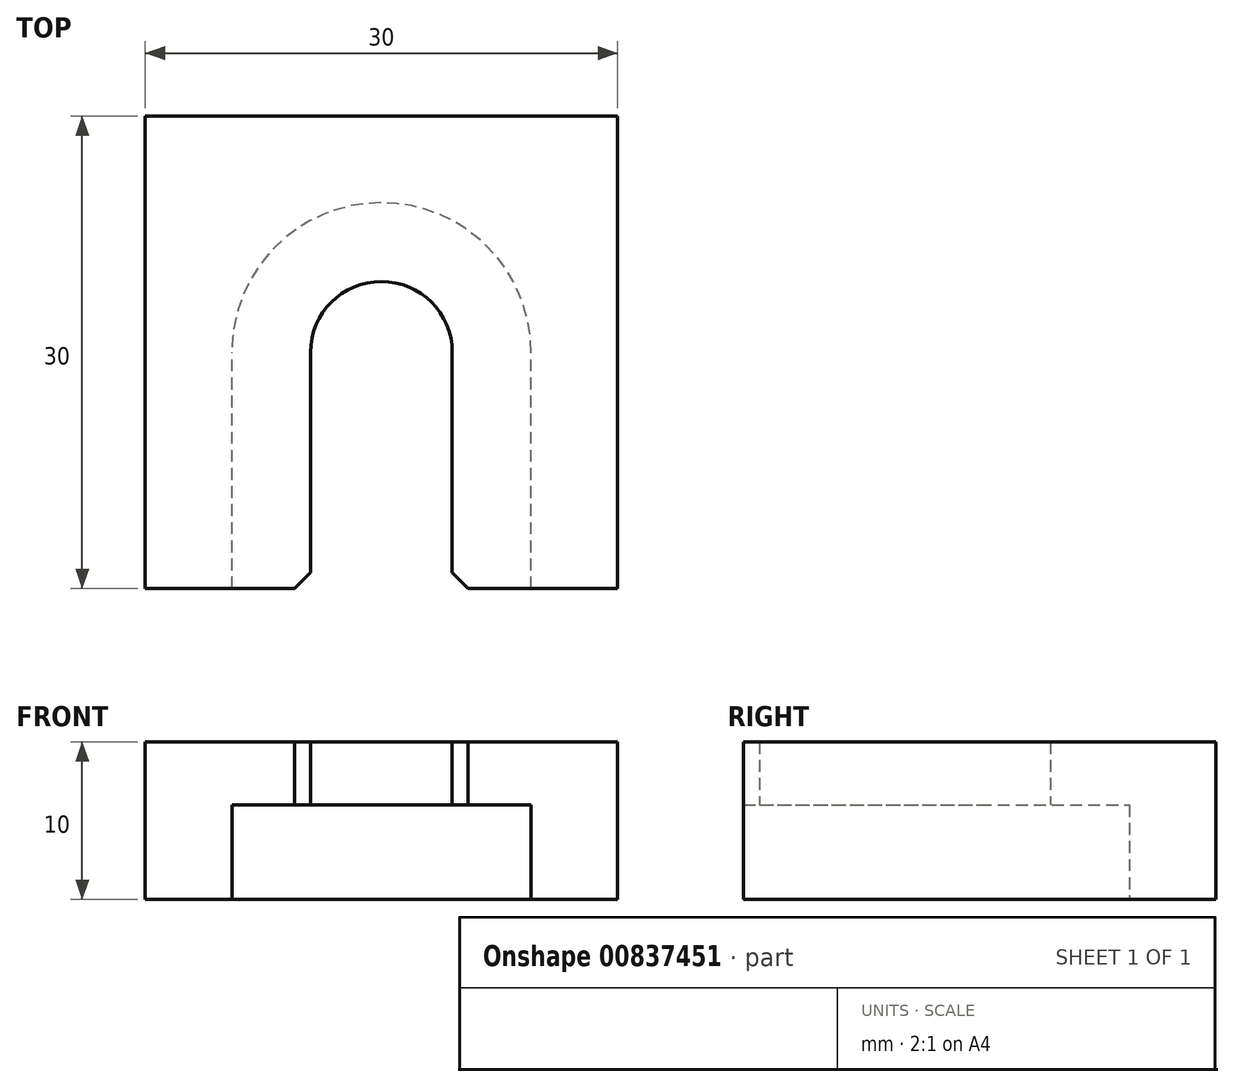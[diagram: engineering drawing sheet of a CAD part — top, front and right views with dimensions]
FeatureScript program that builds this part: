
annotation { "Feature Type Name" : "Feature", "Feature Type Description" : "" }
export const myFeature = defineFeature(function(context is Context, id is Id, definition is map)
    precondition{}
    {
        {
            var Q0;
            Q0=qCreatedBy(makeId("Top.planeOp"),FACE);
            var sketch = newSketch(context, id + "F0", { "sketchPlane" : qUnion([Q0])});
            skLineSegment(sketch, "E0.bottom", {"start": v(-15, 0) * mm, "end": v(-4.5, 0) * mm});
            skLineSegment(sketch, "E0.top", {"start": v(-15, 30) * mm, "end": v(15, 30) * mm});
            skLineSegment(sketch, "E0.left", {"start": v(-15, 0) * mm, "end": v(-15, 30) * mm});
            skLineSegment(sketch, "E0.right", {"start": v(15, 0) * mm, "end": v(15, 30) * mm});
            skLineSegment(sketch, "E1", {"start": v(-4.5, 0) * mm, "end": v(-4.5, 15) * mm});
            skLineSegment(sketch, "E2", {"start": v(4.5, 0) * mm, "end": v(4.5, 15) * mm});
            skArc(sketch, "E3", {"start": v(4.5, 15) * mm, "mid": v(0, 19.5) * mm, "end": v(-4.5, 15) * mm});
            skLineSegment(sketch, "E4.trimOffspring", {"start": v(4.5, 0) * mm, "end": v(15, 0) * mm});
            skSolve(sketch);
        }
        {
            var Q0;
            Q0=makeQuery(id+"F0.imprint","IMPRINT",FACE,{"disambiguationData":[TD([[makeQuery(id+"F0.imprint","IMPRINT",EDGE,{"derivedFrom":sQuery(id+"F0.wireOp",EDGE,"E0.bottom")}),1.0]])]});
            extrude(context, id + "F1", {"entities" : qUnion([Q0]), "depth" : 10 * mm, "offsetDistance" : 25 * mm});
        }
        {
            var Q0;
            Q0=qCreatedBy(makeId("Top.planeOp"),FACE);
            var sketch = newSketch(context, id + "F2", { "sketchPlane" : qUnion([Q0])});
            skLineSegment(sketch, "E5.0", {"start": v(9.5, 0) * mm, "end": v(9.5, 15) * mm});
            skArc(sketch, "E5.1", {"start": v(9.5, 15) * mm, "mid": v(0, 24.5) * mm, "end": v(-9.5, 15) * mm});
            skLineSegment(sketch, "E5.2", {"start": v(-9.5, 0) * mm, "end": v(-9.5, 15) * mm});
            skLineSegment(sketch, "E6.0", {"start": v(-4.5, 0) * mm, "end": v(-4.5, 15) * mm});
            skArc(sketch, "E6.1", {"start": v(4.5, 15) * mm, "mid": v(0, 19.5) * mm, "end": v(-4.5, 15) * mm});
            skLineSegment(sketch, "E6.2", {"start": v(4.5, 0) * mm, "end": v(4.5, 15) * mm});
            skLineSegment(sketch, "E7", {"start": v(-9.5, 0) * mm, "end": v(-4.5, 0) * mm});
            skLineSegment(sketch, "E8", {"start": v(4.5, 0) * mm, "end": v(9.5, 0) * mm});
            skSolve(sketch);
        }
        {
            var Q0;
            Q0=makeQuery(id+"F2.imprint","IMPRINT",FACE,{"disambiguationData":[TD([[makeQuery(id+"F2.imprint","IMPRINT",EDGE,{"derivedFrom":sQuery(id+"F2.wireOp",EDGE,"E5.0")}),1.0]])]});
            extrude(context, id + "F3", {"entities" : qUnion([Q0]), "operationType" : NewBodyOperationType.REMOVE, "depth" : 6 * mm, "offsetDistance" : 25 * mm});
        }
        {
            var Q0;
            Q0=makeQuery(id+"F3.boolean.opBoolean","COPY",EDGE,{"derivedFrom":makeQuery(id+"F3.opExtrude","SWEPT_EDGE",EDGE,{"disambiguationData":[OSD([sQuery(id+"F2.wireOp",EDGE,"E5.2"),sQuery(id+"F2.wireOp",EDGE,"E7")])]})});
            var Q1;
            Q1=makeQuery(id+"F1.opExtrude","SWEPT_EDGE",EDGE,{"disambiguationData":[OSD([sQuery(id+"F0.wireOp",EDGE,"E0.bottom"),sQuery(id+"F0.wireOp",EDGE,"E1")])]});
            var Q2;
            Q2=makeQuery(id+"F3.boolean.opBoolean","COPY",EDGE,{"derivedFrom":makeQuery(id+"F3.opExtrude","SWEPT_EDGE",EDGE,{"disambiguationData":[OSD([sQuery(id+"F2.wireOp",EDGE,"E5.0"),sQuery(id+"F2.wireOp",EDGE,"E8")])]})});
            var Q3;
            Q3=makeQuery(id+"F1.opExtrude","SWEPT_EDGE",EDGE,{"disambiguationData":[OSD([sQuery(id+"F0.wireOp",EDGE,"E2"),sQuery(id+"F0.wireOp",EDGE,"E4.trimOffspring")])]});
            chamfer(context, id + "F4", {"entities" : qUnion([Q0, Q1, Q2, Q3]), "width" : 1 * mm, "tangentPropagation" : true});
        }
    });
